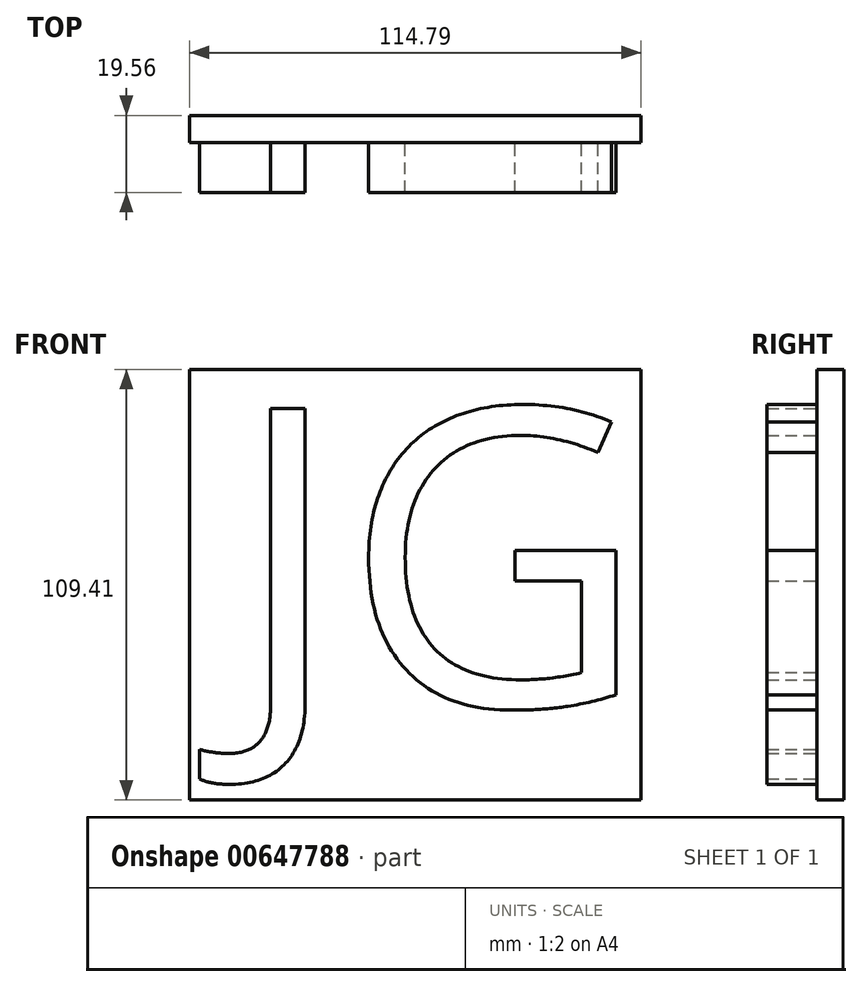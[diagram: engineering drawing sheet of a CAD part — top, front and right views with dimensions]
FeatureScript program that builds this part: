
annotation { "Feature Type Name" : "Feature", "Feature Type Description" : "" }
export const myFeature = defineFeature(function(context is Context, id is Id, definition is map)
    precondition{}
    {
        {
            var Q0;
            Q0=qCreatedBy(makeId("Front.planeOp"),FACE);
            var sketch = newSketch(context, id + "F0", { "sketchPlane" : qUnion([Q0])});
            skText(sketch, "E0", { "text": "JG", "fontName": "OpenSans-Regular.ttf"});
            const initialGuessF0  = {"E0": [-0.05513, -0.03772, 1, 0, 0.0762]};
            skSetInitialGuess(sketch, initialGuessF0);
            skSolve(sketch);
        }
        {
            var Q0;
            Q0 = qSketchRegion(id + "F0", true);
            extrude(context, id + "F1", {"entities" : qUnion([Q0]), "depth" : 12.7 * mm, "offsetDistance" : 25.4 * mm});
        }
        {
            var Q0;
            Q0=qCreatedBy(makeId("Front.planeOp"),FACE);
            var sketch = newSketch(context, id + "F2", { "sketchPlane" : qUnion([Q0])});
            skLineSegment(sketch, "E1.bottom", {"start": v(-65.96, 47.79) * mm, "end": v(48.83, 47.79) * mm});
            skLineSegment(sketch, "E1.top", {"start": v(-65.96, -61.62) * mm, "end": v(48.83, -61.62) * mm});
            skLineSegment(sketch, "E1.left", {"start": v(-65.96, 47.79) * mm, "end": v(-65.96, -61.62) * mm});
            skLineSegment(sketch, "E1.right", {"start": v(48.83, 47.79) * mm, "end": v(48.83, -61.62) * mm});
            skSolve(sketch);
        }
        {
            var Q0;
            Q0 = qSketchRegion(id + "F2", true);
            extrude(context, id + "F3", {"entities" : qUnion([Q0]), "operationType" : NewBodyOperationType.ADD, "oppositeDirection" : true, "depth" : 6.86 * mm, "offsetDistance" : 25.4 * mm});
        }
    });
